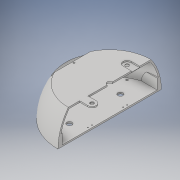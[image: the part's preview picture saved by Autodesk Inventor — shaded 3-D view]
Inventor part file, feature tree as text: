
AUTODESK INVENTOR PART (.ipt)
format: ipt  version: 2019 (Build 230136000, 136)  size: 656,896 bytes
history: native  units: mm
features: sketch x33, extrude x29, other x10, projected_geometry x5, hole x4, reference x2, revolve x1, loft x1, shell x1, mirror x1, fillet x1
ambient origin geometry x8: Origin, YZ Plane, XZ Plane, XY Plane, X Axis, Y Axis, Z Axis, Center Point
bodies: Body1 (feature_tree)
feature tree (88):
  revolve  "Вращение3"
  extrude  "Выдавливание106"  Depth=170.0mm
  extrude  "Выдавливание107"  Depth=100.0mm
  hole  "Отверстие2"  [1 undecoded]
  extrude  "Выдавливание108"  Depth=4.0mm
  hole  "Отверстие3"  [1 undecoded]
  hole  "Отверстие4"  [1 undecoded]
  hole  "Отверстие5"  [1 undecoded]
  extrude  "Выдавливание109"  TaperAngle=0.0deg  [1 undecoded]
  sketch  "Эскиз132"
  extrude  "Выдавливание110"  Depth=130.0mm TaperAngle=0.0deg
  extrude  "Выдавливание111"  Depth=5.0mm
  extrude  "Выдавливание113"  Depth=2.0mm
  extrude  "Выдавливание114"  Depth=2.0mm
  other  "РабПлоскость27"
  extrude  "Выдавливание115"  Depth=2.0mm
  sketch  "Эскиз4"
  other  "РабПлоскость1"
  sketch  "Эскиз5"
  loft  "Лофт1"
  extrude  "Выдавливание2"  Depth=10.0mm TaperAngle=0.0deg
  shell  "Оболочка1"  Thickness=10.0mm
  sketch  "Эскиз21"
  extrude  "Выдавливание15"  Depth=143.802871mm
  extrude  "Выдавливание16"  TaperAngle=0.0deg  [1 undecoded]
  other  "РабПлоскость7"
  sketch  "Эскиз23"
  extrude  "Выдавливание17"  Depth=1.0mm TaperAngle=0.0deg
  extrude  "Выдавливание18"  Depth=5.0mm
  sketch  "Эскиз24"
  extrude  "Выдавливание19"  Depth=5.0mm
  extrude  "Выдавливание20"  Depth=2.0mm
  extrude  "Выдавливание21"  Depth=2.0mm
  mirror  "Зеркальное отражение2"
  other  "РабПлоскость12"
  sketch  "Эскиз42"
  extrude  "Выдавливание57"  Depth=5.0mm
  sketch  "Эскиз84"
  extrude  "Выдавливание75"  Depth=1.0mm TaperAngle=0.0deg
  extrude  "Выдавливание76"  Depth=3.0mm
  extrude  "Выдавливание77"  Depth=2.0mm
  extrude  "Выдавливание95"  Depth=6.0mm
  extrude  "Выдавливание96"  Depth=1.0mm TaperAngle=0.0deg
  extrude  "Выдавливание97"  Depth=2.0mm
  fillet  "Сопряжение3"  Radius=2.0mm
  extrude  "Выдавливание98"  Depth=2.0mm
  extrude  "Выдавливание101"  Depth=5.0mm
  other  "РабПлоскость25"
  extrude  "Выдавливание102"  Depth=1.0mm TaperAngle=0.0deg
  other  "РабПлоскость26"
  extrude  "Выдавливание103"  Depth=4.0mm
  extrude  "Выдавливание104"  Depth=2.0mm
  sketch  "Эскиз6"
  projected_geometry  "Спроецированная петля1"
  sketch  "Эскиз22"
  sketch  "Эскиз25"
  sketch  "Эскиз61"
  sketch  "Эскиз87"
  sketch  "Эскиз109"
  sketch  "Эскиз110"
  projected_geometry  "Спроецированная петля42"
  sketch  "Эскиз111"
  projected_geometry  "Спроецированная петля43"
  sketch  "Эскиз114"
  sketch  "Эскиз117"
  sketch  "Эскиз118"
  reference  "Ссылка1"
  reference  "Ссылка2"
  sketch  "Эскиз119"
  sketch  "Эскиз120"
  sketch  "Эскиз121"
  other  "Твердое тело3"
  sketch  "Эскиз124"
  sketch  "Эскиз125"
  sketch  "Эскиз126"
  sketch  "Эскиз127"
  sketch  "Эскиз128"
  sketch  "Эскиз129"
  sketch  "Эскиз130"
  sketch  "Эскиз131"
  projected_geometry  "Спроецированная петля45"
  projected_geometry  "Спроецированная петля46"
  sketch  "Эскиз133"
  sketch  "Эскиз134"
  sketch  "Эскиз135"
  other  "<userpath>\Desktop\САПР\Работы\ПД\робот\робот - сборка фулл.iam"
  other  "робот - сборка фулл.iam"
  other  "крепление-стенки:1"
note: 6 required parameter values undecoded (feature->parameter linkage not recoverable at this tier; creation-order binding heuristic only, values carry confidence <= 0.55)
